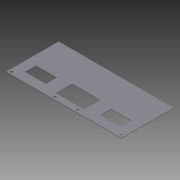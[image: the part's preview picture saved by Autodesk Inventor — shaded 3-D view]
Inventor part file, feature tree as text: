
AUTODESK INVENTOR PART (.ipt)
format: ipt  version: 2012 (Build 160160000, 160)  size: 144,896 bytes
history: native  units: mm
features: reference x5, sketch x3, extrude x2, hole x1
ambient origin geometry x8: Origin, YZ Plane, XZ Plane, XY Plane, X Axis, Y Axis, Z Axis, Center Point
bodies: Solid1 (feature_tree)
feature tree (11):
  extrude  "Extrusion1"  Depth=88.9mm
  extrude  "Extrusion4"  Depth=16.256mm
  hole  "Hole5"  [1 undecoded]
  sketch  "Sketch1"  dims[d0=195.58mm d1=88.9mm]
  sketch  "Sketch9"  dims[d2=0.762mm d3=0.0mm d105=16.256mm]
  sketch  "Sketch10"  dims[d106=19.05mm d107=35.56mm d108=16.256mm d109=19.05mm d110=35.56mm d111=15.24mm d112=15.24mm d113=48.26mm d114=27.94mm d115=73.66mm d116=73.66mm d117=10.16mm d118=25.4mm d119=0.0mm d120=4.318mm d121=19.05mm d122=8.4328mm d123=6.35mm d124=14.3117mm d125=25.4mm d126=20.594885mm d127=81.28mm d128=55.88mm d129=55.88mm d130=81.28mm d131=81.28mm d132=55.88mm d133=55.88mm d134=81.28mm]
  reference  "Reference8"
  reference  "Reference9"
  reference  "Reference10"
  reference  "Reference11"
  reference  "Reference12"
note: 1 required parameter value undecoded (feature->parameter linkage not recoverable at this tier; creation-order binding heuristic only, values carry confidence <= 0.55)
